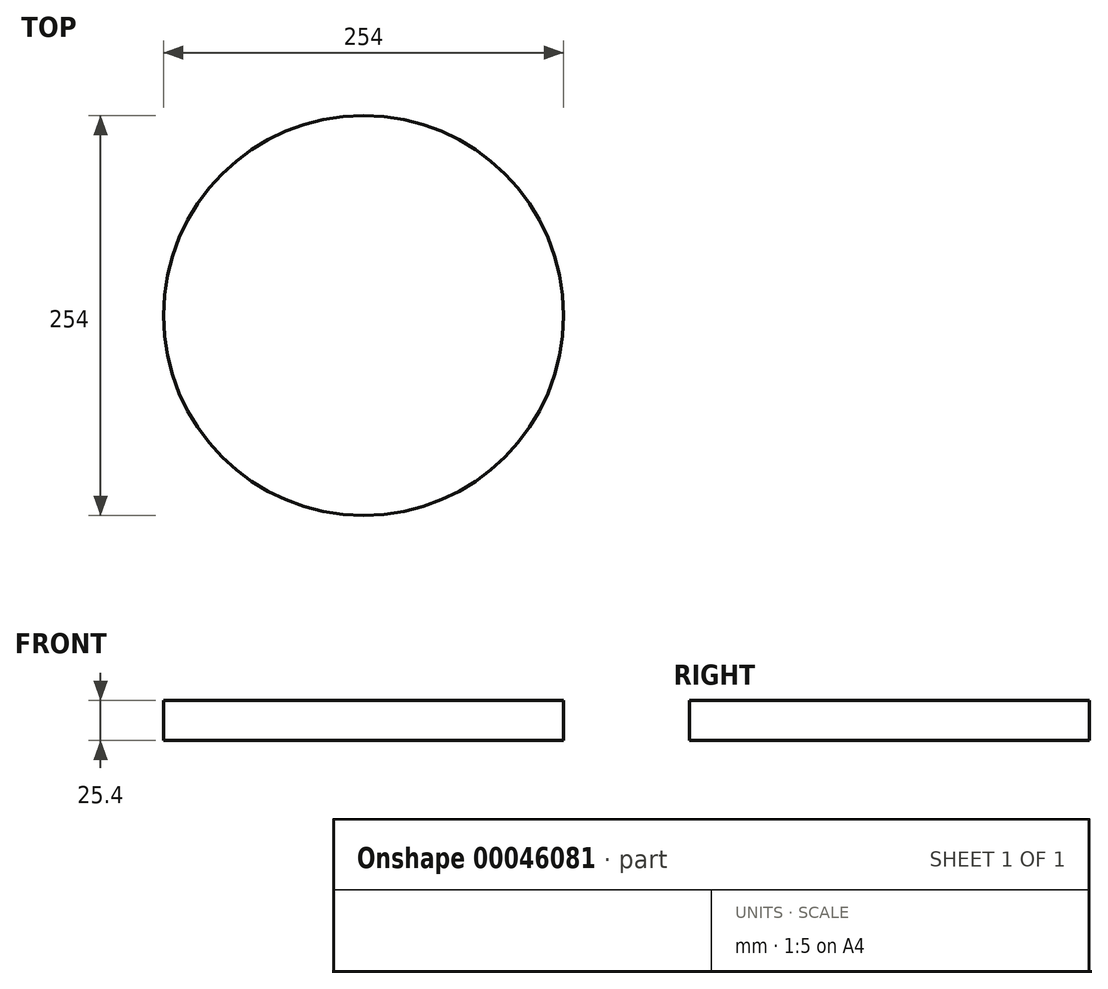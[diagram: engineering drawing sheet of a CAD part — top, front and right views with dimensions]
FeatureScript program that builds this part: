
annotation { "Feature Type Name" : "Feature", "Feature Type Description" : "" }
export const myFeature = defineFeature(function(context is Context, id is Id, definition is map)
    precondition{}
    {
        {
            var Q0;
            Q0=qCreatedBy(makeId("Top.planeOp"),FACE);
            var sketch = newSketch(context, id + "F0", { "sketchPlane" : qUnion([Q0])});
            skCircle(sketch, "E0", {"center": v(0, 0) * mm, "radius": 127 * mm});
            skSolve(sketch);
        }
        {
            var Q0;
            Q0 = qSketchRegion(id + "F0", true);
            extrude(context, id + "F1", {"entities" : qUnion([Q0]), "endBound" : BoundingType.SYMMETRIC, "depth" : 25.4 * mm});
        }
    });
